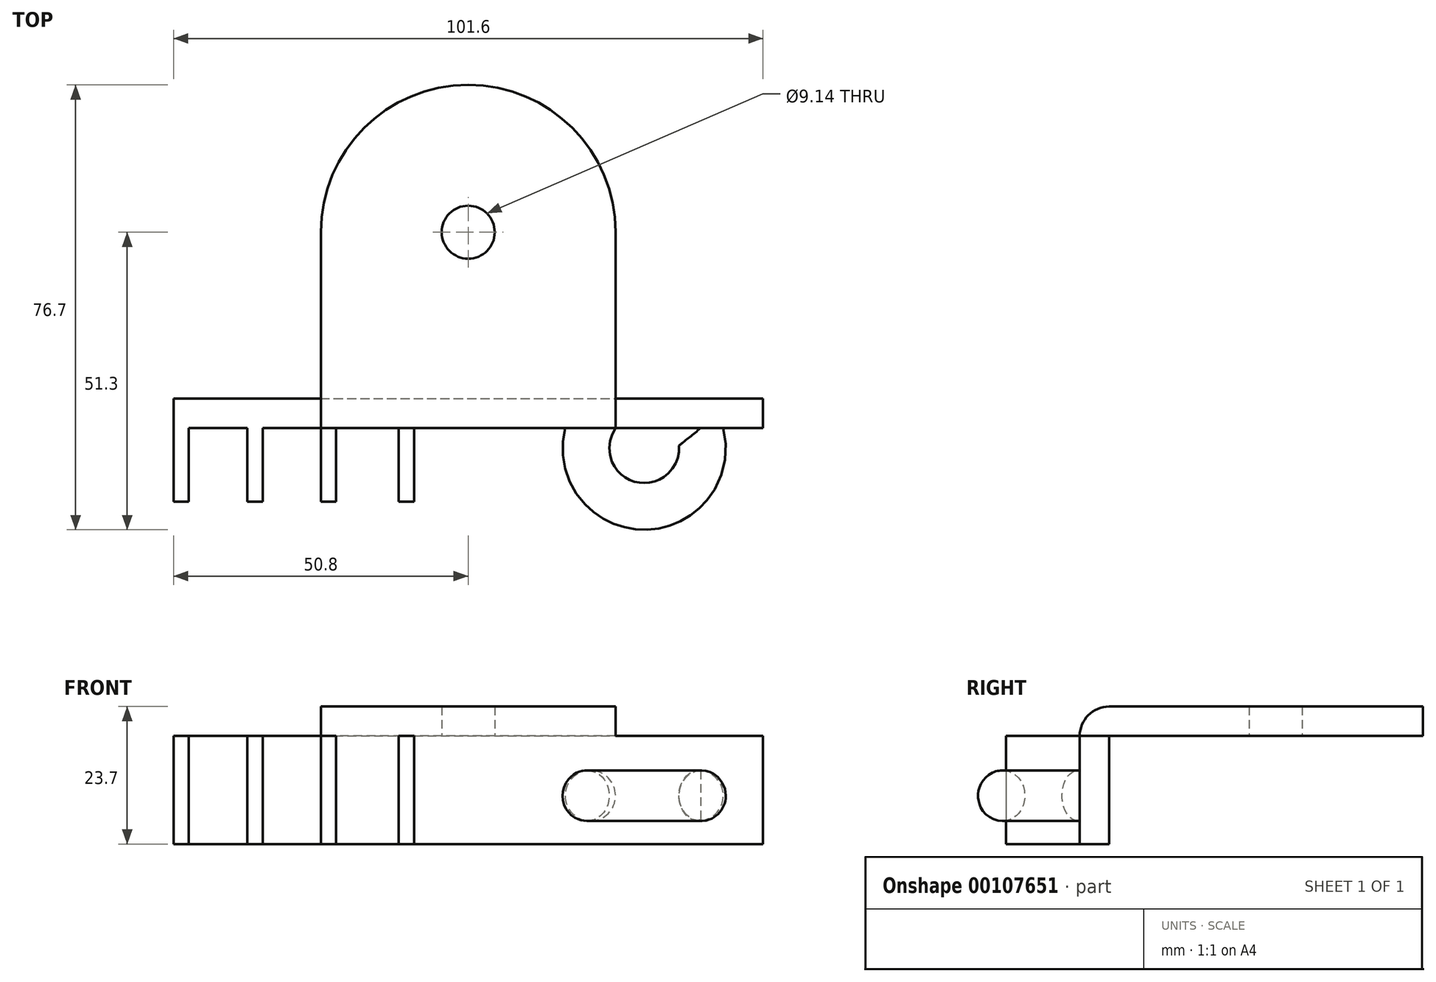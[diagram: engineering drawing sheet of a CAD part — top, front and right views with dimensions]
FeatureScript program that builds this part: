
annotation { "Feature Type Name" : "Feature", "Feature Type Description" : "" }
export const myFeature = defineFeature(function(context is Context, id is Id, definition is map)
    precondition{}
    {
        {
            var Q0;
            Q0=qCreatedBy(makeId("Top.planeOp"),FACE);
            var sketch = newSketch(context, id + "F0", { "sketchPlane" : qUnion([Q0])});
            skCircle(sketch, "E0", {"center": v(0, 0) * mm, "radius": 25.4 * mm});
            skCircle(sketch, "E1", {"center": v(0, 0) * mm, "radius": 4.57 * mm});
            skLineSegment(sketch, "E2", {"start": v(-25.4, 0) * mm, "end": v(-25.4, -28.7) * mm});
            skLineSegment(sketch, "E3", {"start": v(25.4, 0) * mm, "end": v(25.4, -28.7) * mm});
            skLineSegment(sketch, "E4", {"start": v(-25.4, -28.7) * mm, "end": v(25.4, -28.7) * mm});
            skLineSegment(sketch, "E5", {"start": v(0, -4.57) * mm, "end": v(0, -28.7) * mm, "construction": true});
            skLineSegment(sketch, "E6", {"start": v(25.4, -28.7) * mm, "end": v(21.08, -28.7) * mm, "construction": true});
            skSolve(sketch);
        }
        {
            var Q0;
            Q0=makeQuery(id+"F0.imprint","IMPRINT",FACE,{"disambiguationData":[TD([[makeQuery(id+"F0.imprint","IMPRINT",EDGE,{"derivedFrom":sQuery(id+"F0.wireOp",EDGE,"E1")}),-1.0]])]});
            var Q1;
            {var subQ0=sQuery(id+"F0.wireOp",EDGE,"E2");Q1=makeQuery(id+"F0.imprint","IMPRINT",FACE,{"disambiguationData":[TD([[makeQuery(id+"F0.imprint","IMPRINT",EDGE,{"derivedFrom":subQ0}),1.0]])]});}
            extrude(context, id + "F1", {"entities" : qUnion([Q0, Q1]), "depth" : 5.08 * mm});
        }
        {
            var Q0;
            Q0=makeQuery(id+"F1.opExtrude","SWEPT_FACE",FACE,{"disambiguationData":[OSD([sQuery(id+"F0.wireOp",EDGE,"E4")])]});
            var sketch = newSketch(context, id + "F2", { "sketchPlane" : qUnion([Q0])});
            skLineSegment(sketch, "E7", {"start": v(-25.4, 0) * mm, "end": v(-50.8, 0) * mm});
            skLineSegment(sketch, "E8", {"start": v(25.4, 0) * mm, "end": v(50.8, 0) * mm});
            skLineSegment(sketch, "E9", {"start": v(-50.8, 0) * mm, "end": v(-50.8, -18.62) * mm});
            skLineSegment(sketch, "E10", {"start": v(50.8, 0) * mm, "end": v(50.8, -18.62) * mm});
            skLineSegment(sketch, "E11", {"start": v(-50.8, -18.62) * mm, "end": v(50.8, -18.62) * mm});
            skSolve(sketch);
        }
        {
            var Q0;
            Q0=makeQuery(id+"F2.imprint","IMPRINT",FACE,{"disambiguationData":[TD([[makeQuery(id+"F2.imprint","IMPRINT",EDGE,{"derivedFrom":sQuery(id+"F2.wireOp",EDGE,"63f74Tt5-iKsr-5Ox6-La0o-mpZi10Kc4vKe")}),1.0]])]});
            var Q1;
            {var subQ0=sQuery(id+"F0.wireOp",EDGE,"E4");Q1=makeQuery(id+"F2.imprint","IMPRINT",FACE,{"disambiguationData":[TD([[makeQuery(id+"F2.imprint","IMPRINT",EDGE,{"derivedFrom":makeQuery(id+"F1.opExtrude","CAP_EDGE",EDGE,{"disambiguationData":[OSD([subQ0])],"isStart":true})}),1.0]])]});}
            var Q2;
            Q2=makeQuery(id+"F2.imprint","IMPRINT",FACE,{"disambiguationData":[TD([[makeQuery(id+"F2.imprint","IMPRINT",EDGE,{"derivedFrom":sQuery(id+"F2.wireOp",EDGE,"E7")}),1.0]])]});
            extrude(context, id + "F3", {"entities" : qUnion([Q0, Q1, Q2]), "operationType" : NewBodyOperationType.ADD, "depth" : 5.08 * mm});
        }
        {
            var Q0;
            Q0=makeQuery(id+"F3.opExtrude","CAP_FACE",FACE,{"disambiguationData":[OSD([sQuery(id+"F0.wireOp",EDGE,"E2"),sQuery(id+"F0.wireOp",EDGE,"E3"),sQuery(id+"F0.wireOp",EDGE,"E4"),sQuery(id+"F2.wireOp",EDGE,"63f74Tt5-iKsr-5Ox6-La0o-mpZi10Kc4vKe"),sQuery(id+"F2.wireOp",EDGE,"d2xyoYXC-B8HI-hh2I-1Yq0-RyRUqkECwTI4"),sQuery(id+"F2.wireOp",EDGE,"3O3DADeE-7ynP-DEnl-VSnk-NbRCMQ3cdLog")])],"isStart":false});
            var sketch = newSketch(context, id + "F4", { "sketchPlane" : qUnion([Q0])});
            skCircle(sketch, "E12", {"center": v(21.05, -10.29) * mm, "radius": 4.35 * mm});
            skLineSegment(sketch, "E13", {"start": v(25.4, 0) * mm, "end": v(25.4, -10.29) * mm, "construction": true});
            skLineSegment(sketch, "E14", {"start": v(21.05, -10.29) * mm, "end": v(25.4, -10.29) * mm, "construction": true});
            skSolve(sketch);
        }
        {
            var Q0;
            {var subQ0=sQuery(id+"F0.wireOp",EDGE,"E4");Q0=makeQuery(id+"F3.boolean.opBoolean","MERGE",FACE,{"derivedFrom":[makeQuery(id+"F1.opExtrude","CAP_FACE",FACE,{"disambiguationData":[OSD([sQuery(id+"F0.wireOp",EDGE,"E0"),sQuery(id+"F0.wireOp",EDGE,"E1"),sQuery(id+"F0.wireOp",EDGE,"E2"),sQuery(id+"F0.wireOp",EDGE,"E3"),subQ0])],"isStart":false}),makeQuery(id+"F3.opExtrude","SWEPT_FACE",FACE,{"disambiguationData":[OSD([subQ0])]})]});}
            var sketch = newSketch(context, id + "F5", { "sketchPlane" : qUnion([Q0])});
            skLineSegment(sketch, "E15", {"start": v(25.4, -33.78) * mm, "end": v(20.57, -33.78) * mm, "construction": true});
            skArc(sketch, "E16", {"start": v(20.57, -33.78) * mm, "mid": v(30.33, -47.59) * mm, "end": v(40.1, -33.78) * mm});
            skPoint(sketch, "E16.endSnap0", {"position": v(22.99, -33.78) * mm});
            skSolve(sketch);
        }
        {
            var Q0;
            Q0=makeQuery(id+"F4.imprint","IMPRINT",FACE,{"disambiguationData":[TD([[makeQuery(id+"F4.imprint","IMPRINT",EDGE,{"derivedFrom":sQuery(id+"F4.wireOp",EDGE,"E12")}),1.0]])]});
            var Q1;
            Q1 = qConstructionFilter(qBodyType(qCreatedBy(id + "F5" ,EDGE), BodyType.WIRE), ConstructionObject.NO);
            sweep(context, id + "F6", {"operationType" : NewBodyOperationType.ADD, "profiles" : qUnion([Q0]), "path" : qUnion([Q1])});
        }
        {
            var Q0;
            Q0=makeQuery(id+"F3.opExtrude","CAP_FACE",FACE,{"disambiguationData":[OSD([sQuery(id+"F0.wireOp",EDGE,"E2"),sQuery(id+"F0.wireOp",EDGE,"E3"),sQuery(id+"F0.wireOp",EDGE,"E4"),sQuery(id+"F2.wireOp",EDGE,"E7"),sQuery(id+"F2.wireOp",EDGE,"E8"),sQuery(id+"F2.wireOp",EDGE,"E9"),sQuery(id+"F2.wireOp",EDGE,"E10"),sQuery(id+"F2.wireOp",EDGE,"E11")])],"isStart":false});
            var sketch = newSketch(context, id + "F7", { "sketchPlane" : qUnion([Q0])});
            skLineSegment(sketch, "E17.bottom", {"start": v(-50.8, 0) * mm, "end": v(-48.2, 0) * mm});
            skLineSegment(sketch, "E17.top", {"start": v(-50.8, -18.62) * mm, "end": v(-48.2, -18.62) * mm});
            skLineSegment(sketch, "E17.left", {"start": v(-50.8, 0) * mm, "end": v(-50.8, -18.62) * mm});
            skLineSegment(sketch, "E17.right", {"start": v(-48.2, 0) * mm, "end": v(-48.2, -18.62) * mm});
            skLineSegment(sketch, "E18.bottom", {"start": v(-38.1, 0) * mm, "end": v(-35.46, 0) * mm});
            skLineSegment(sketch, "E18.top", {"start": v(-38.1, -18.62) * mm, "end": v(-35.46, -18.62) * mm});
            skLineSegment(sketch, "E18.left", {"start": v(-38.1, 0) * mm, "end": v(-38.1, -18.62) * mm});
            skLineSegment(sketch, "E18.right", {"start": v(-35.46, 0) * mm, "end": v(-35.46, -18.62) * mm});
            skLineSegment(sketch, "E19.bottom", {"start": v(-25.4, 0) * mm, "end": v(-22.8, 0) * mm});
            skLineSegment(sketch, "E19.top", {"start": v(-25.4, -18.62) * mm, "end": v(-22.8, -18.62) * mm});
            skLineSegment(sketch, "E19.left", {"start": v(-25.4, 0) * mm, "end": v(-25.4, -18.62) * mm});
            skLineSegment(sketch, "E19.right", {"start": v(-22.8, 0) * mm, "end": v(-22.8, -18.62) * mm});
            skLineSegment(sketch, "E20.bottom", {"start": v(-12, 0) * mm, "end": v(-9.32, 0) * mm});
            skLineSegment(sketch, "E20.top", {"start": v(-12, -18.62) * mm, "end": v(-9.32, -18.62) * mm});
            skLineSegment(sketch, "E20.left", {"start": v(-12, 0) * mm, "end": v(-12, -18.62) * mm});
            skLineSegment(sketch, "E20.right", {"start": v(-9.32, 0) * mm, "end": v(-9.32, -18.62) * mm});
            skSolve(sketch);
        }
        {
            var Q0;
            Q0 = qSketchRegion(id + "F7", true);
            extrude(context, id + "F8", {"entities" : qUnion([Q0]), "operationType" : NewBodyOperationType.ADD, "depth" : 12.7 * mm});
        }
        {
            var Q0;
            Q0=makeQuery(id+"F3.opExtrude","CAP_EDGE",EDGE,{"disambiguationData":[OSD([sQuery(id+"F0.wireOp",EDGE,"E4")])],"isStart":false});
            fillet(context, id + "F9", {"entities" : qUnion([Q0]), "radius" : 5.08 * mm, "tangentPropagation" : true, "allowEdgeOverflow" : false});
        }
    });
